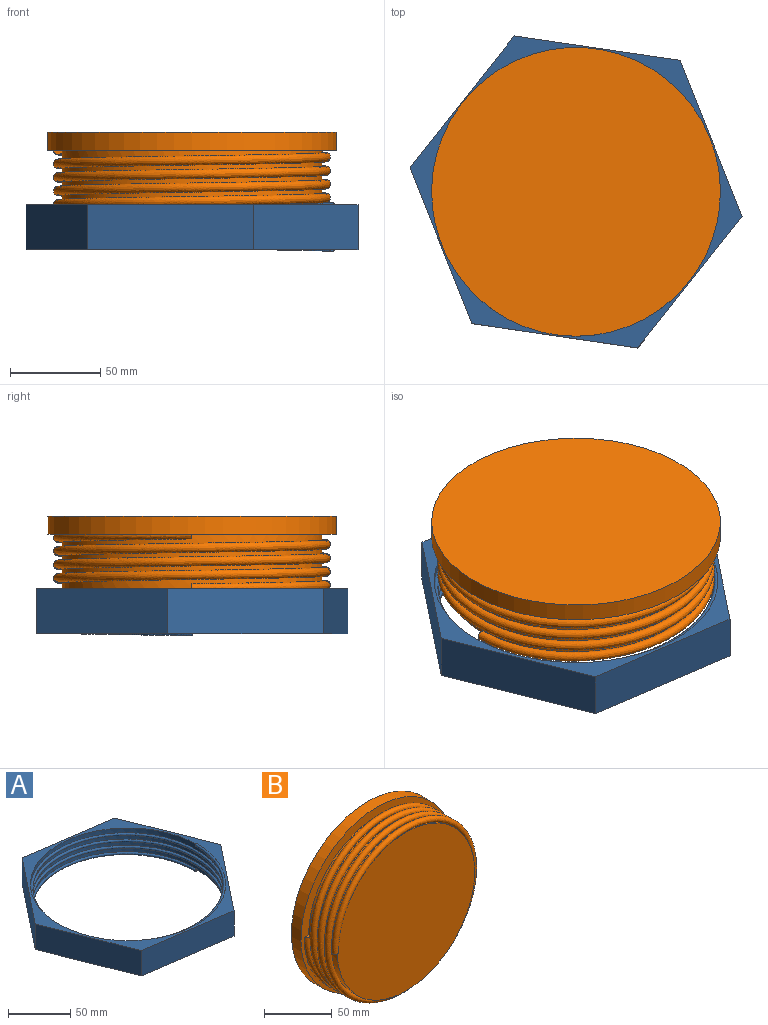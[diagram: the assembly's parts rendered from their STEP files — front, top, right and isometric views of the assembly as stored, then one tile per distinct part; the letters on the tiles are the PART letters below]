
ASSEMBLY  parts=2 mates=1
PART A: 12 faces, bbox 183.9x172.8x27.2 mm
  f0: plane 183.88x172.8mm, normal (0,0,1), area 3040.4mm2, adj f1,f2,f3,f4,f5,f6,f7,f9
  f1: plane 72.84x57.71mm, normal (0.78,-0.62,0), area 2323.3mm2, adj f0,f2,f6,f8
  f2: plane 86.4x34.23mm, normal (0.93,0.37,0), area 2323.3mm2, adj f0,f1,f3,f8
  f3: plane 91.94x25mm, normal (0.15,0.99,0), area 2323.3mm2, adj f0,f2,f4,f8
  f4: plane 72.84x57.71mm, normal (-0.78,0.62,0), area 2323.3mm2, adj f0,f3,f5,f8
  f5: plane 86.4x34.23mm, normal (-0.93,-0.37,0), area 2323.3mm2, adj f0,f4,f6,f8
  f6: plane 91.94x25mm, normal (-0.15,-0.99,0), area 2323.3mm2, adj f0,f1,f5,f8
  f7: cylinder r=78.57mm len=157.14mm, axis (0,0,-1), area 10236.1mm2, adj f0,f8,f9,f10,f11
  f8: plane 183.88x172.8mm, normal (0,0,-1), area 3040.4mm2, adj f1,f2,f3,f4,f5,f6,f7,f9
  f9: bspline ~157.32x157.26mm, area 11396.7mm2, adj f0,f7,f8,f10,f11
  f10: plane 2.21x2.21mm, normal (0,-1,0), area 3.8mm2, adj f7,f8,f9
  f11: plane 2.21x2.21mm, normal (0,1,0), area 3.8mm2, adj f0,f7,f9
PART B: 8 faces, bbox 160x45.1x160 mm
  f0: plane 4.72x2.51mm, normal (0,0,1), area 9.7mm2, adj f1,f3,f5
  f1: bspline ~153.41x153.41mm, area 24079.4mm2, adj f0,f2,f3,f4,f5
  f2: plane 5.09x5.09mm, normal (0,0,-1), area 20mm2, adj f1,f3,f4
  f3: cylinder r=71.99mm len=143.98mm, axis (0,1,0), area 8846.9mm2, adj f0,f1,f2,f4,f5
  f4: plane 143.98x143.98mm, normal (0,-1,0), area 16260.9mm2, adj f1,f2,f3
  f5: plane 159.97x159.97mm, normal (0,-1,0), area 3165.8mm2, adj f0,f1,f3,f6
  f6: cylinder r=79.99mm len=159.97mm, axis (0,-1,0), area 5025.7mm2, adj f5,f7
  f7: plane 159.97x159.97mm, normal (0,1,0), area 20099.7mm2, adj f6
PLACE A t=(356.89,184.5,-44.83)mm
PLACE B rot(axis=(1,0,0),90deg) t=(356.89,184.5,10.17)mm
MATE cylindrical B.f3 <-> A.f7  axis (0,0,-1) through (356.89,184.5,-19.83)mm
